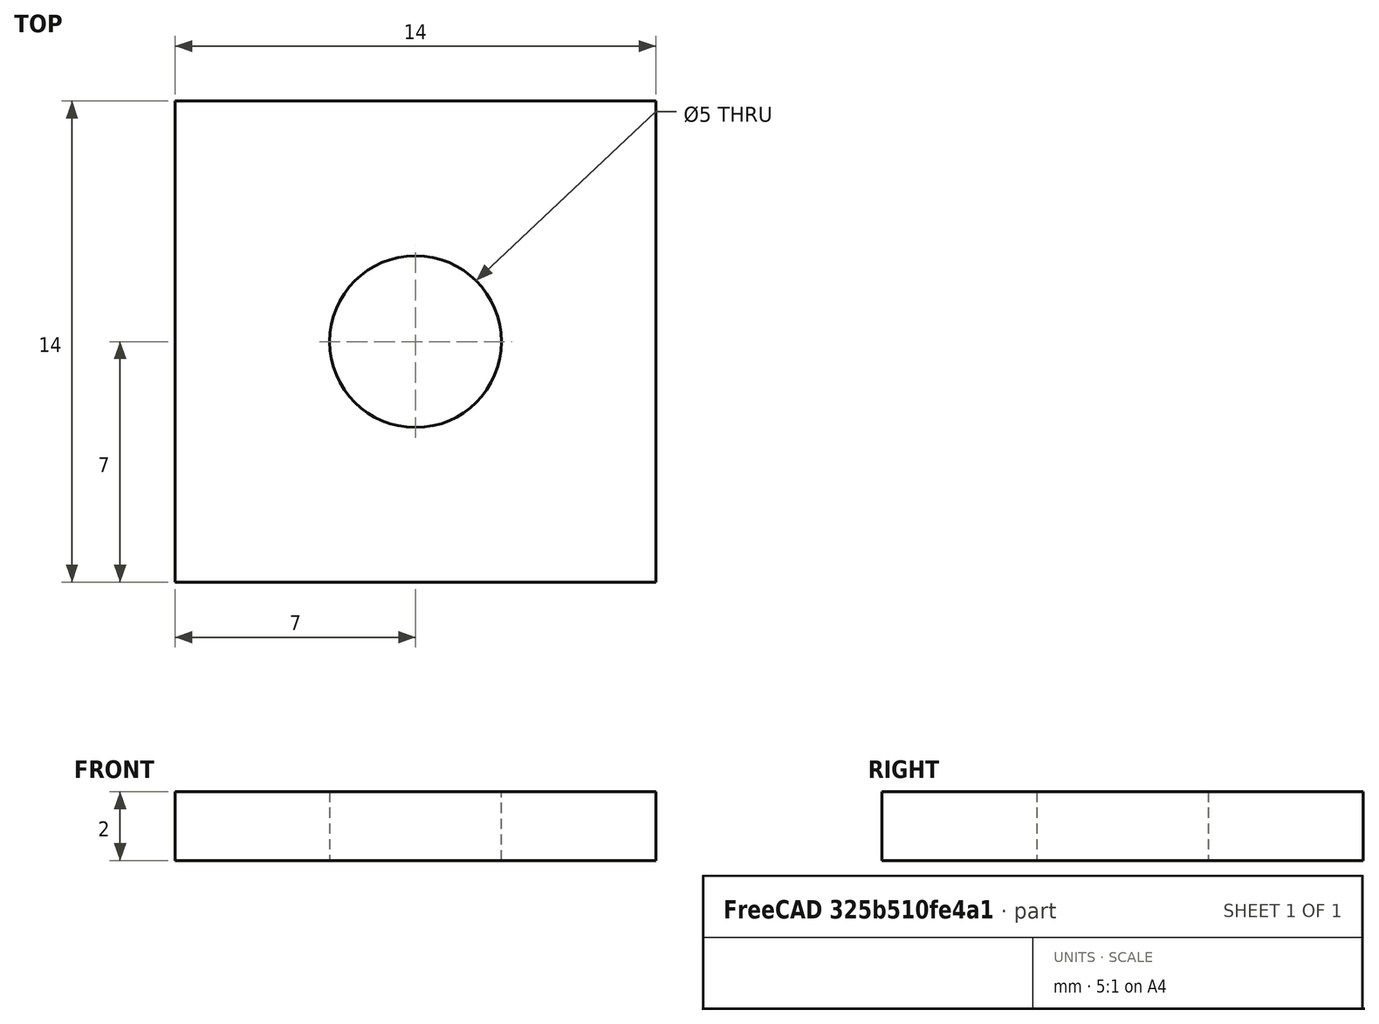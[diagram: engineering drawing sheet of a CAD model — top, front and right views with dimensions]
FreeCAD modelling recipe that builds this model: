
FCSTD DOCUMENT  (FreeCAD 0.18R16110 (Git))
Label: handle
License: All rights reserved
LicenseURL: http://en.wikipedia.org/wiki/All_rights_reserved
objects: Sketcher::SketchObject×1, Part::Extrusion×1
note: 2 computed .brp shape members not serialized (recipe doc carries the construction recipe); baked Part::Feature solids carry a one-line shape summary decoded from their .brp

FEATURE [Sketcher::SketchObject] Sketch
  sketch-geometry (5):
    g0: LineSegment StartX=-7 StartY=7 StartZ=0 EndX=7 EndY=7 EndZ=0
    g1: LineSegment StartX=7 StartY=7 StartZ=0 EndX=7 EndY=-7 EndZ=0
    g2: LineSegment StartX=7 StartY=-7 StartZ=0 EndX=-7 EndY=-7 EndZ=0
    g3: LineSegment StartX=-7 StartY=-7 StartZ=0 EndX=-7 EndY=7 EndZ=0
    g4: Circle CenterX=0 CenterY=0 CenterZ=0 NormalX=0 NormalY=0 NormalZ=1 AngleXU=0 Radius=2.5
  constraints (12):
    c: Coincident(g0,g1)
    c: Coincident(g1,g2)
    c: Coincident(g2,g3)
    c: Coincident(g3,g0)
    c: Horizontal(g2)
    c: Vertical(g1)
    c: Symmetric(g0,g0,g-2)
    c: Symmetric(g0,g2,g-1)
    c: Equal(g0,g3)
    c: Distance(g0) = 14
    c: Coincident(g4,g-1)
    c: Radius(g4) = 2.5
FEATURE [Part::Extrusion] Extrude
  Base = -> Sketch
  Dir = (0,0,1)
  DirMode = 2
  FaceMakerClass = Part::FaceMakerBullseye
  LengthFwd = 2
  LengthRev = 0
  Solid = true
  Symmetric = false
